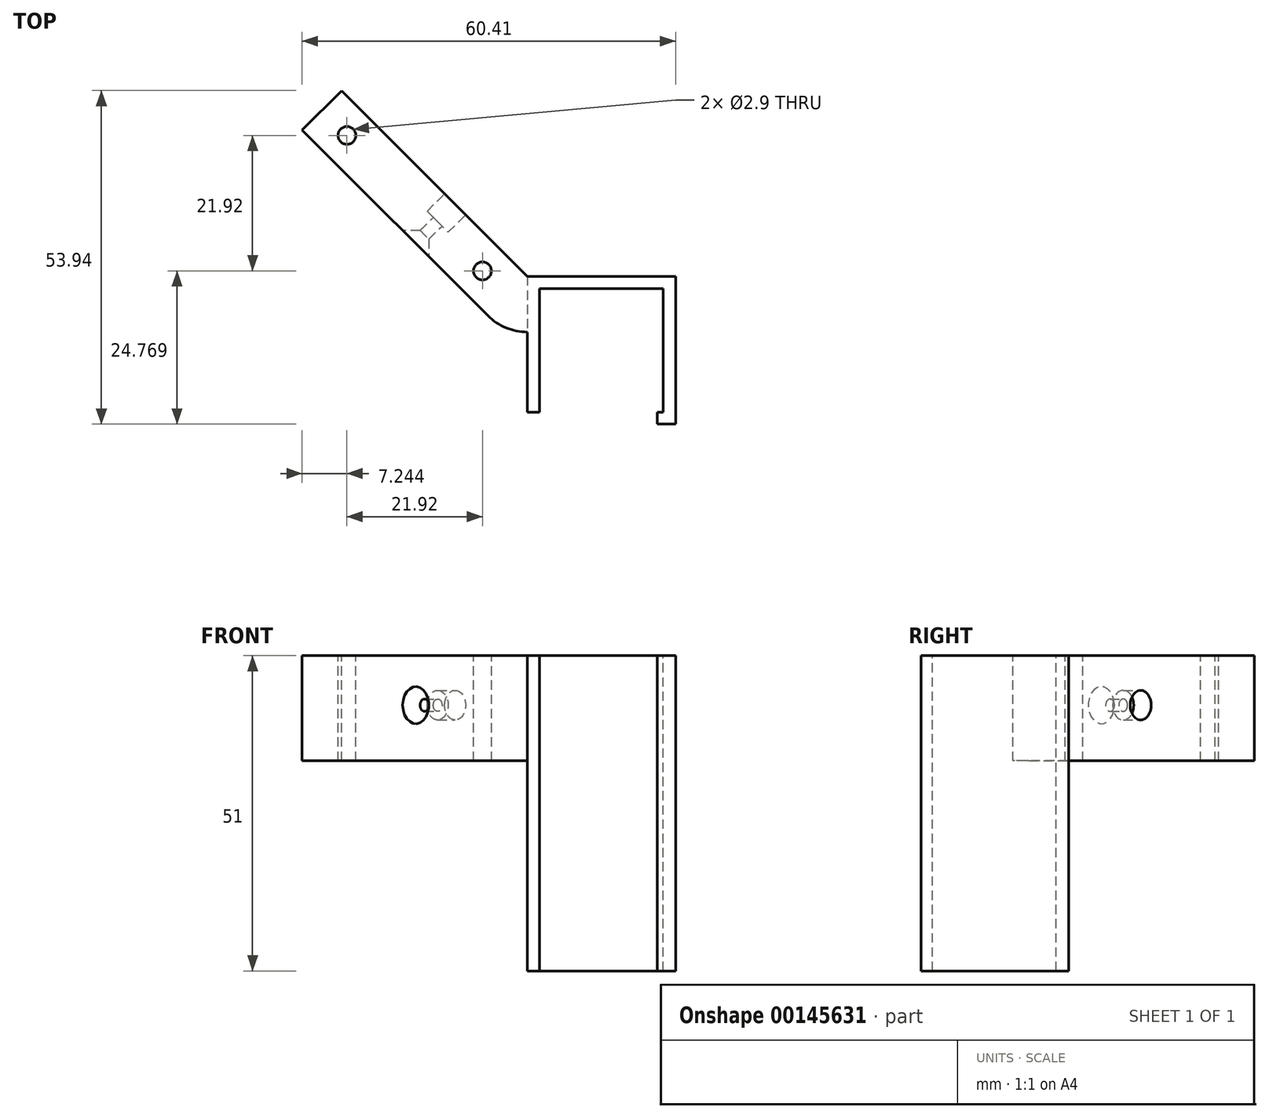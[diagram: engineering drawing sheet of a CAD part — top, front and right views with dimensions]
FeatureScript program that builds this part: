
annotation { "Feature Type Name" : "Feature", "Feature Type Description" : "" }
export const myFeature = defineFeature(function(context is Context, id is Id, definition is map)
    precondition{}
    {
        {
            var Q0;
            Q0=qCreatedBy(makeId("Top.planeOp"),FACE);
            var sketch = newSketch(context, id + "F0", { "sketchPlane" : qUnion([Q0])});
            skLineSegment(sketch, "E0", {"start": v(0.11, 9.4) * mm, "end": v(0.11, 0.4) * mm});
            skLineSegment(sketch, "E1", {"start": v(0.11, 0.4) * mm, "end": v(0.11, -12.6) * mm});
            skLineSegment(sketch, "E2", {"start": v(0.11, -12.6) * mm, "end": v(2.11, -12.6) * mm});
            skLineSegment(sketch, "E3", {"start": v(2.11, -12.6) * mm, "end": v(2.11, 7.4) * mm});
            skLineSegment(sketch, "E4", {"start": v(2.11, 7.4) * mm, "end": v(22.11, 7.4) * mm});
            skLineSegment(sketch, "E5", {"start": v(22.11, 7.4) * mm, "end": v(22.11, -12.6) * mm});
            skLineSegment(sketch, "E6", {"start": v(24.11, -12.6) * mm, "end": v(24.11, 9.4) * mm});
            skLineSegment(sketch, "E7", {"start": v(24.11, 9.4) * mm, "end": v(0.11, 9.4) * mm});
            skLineSegment(sketch, "E8", {"start": v(22.11, -12.6) * mm, "end": v(21.11, -12.6) * mm});
            skLineSegment(sketch, "E9", {"start": v(21.11, -12.6) * mm, "end": v(21.11, -14.48) * mm});
            skLineSegment(sketch, "E10", {"start": v(21.11, -14.48) * mm, "end": v(24.11, -14.48) * mm});
            skLineSegment(sketch, "E11", {"start": v(24.11, -14.48) * mm, "end": v(24.11, -12.6) * mm});
            skLineSegment(sketch, "E12", {"start": v(-29.94, 39.46) * mm, "end": v(0.11, 9.4) * mm});
            skLineSegment(sketch, "E13", {"start": v(0.11, 9.4) * mm, "end": v(-6.25, 3.04) * mm});
            skLineSegment(sketch, "E14", {"start": v(-6.25, 3.04) * mm, "end": v(-36.3, 33.1) * mm});
            skLineSegment(sketch, "E15", {"start": v(-36.3, 33.1) * mm, "end": v(-29.94, 39.46) * mm});
            skLineSegment(sketch, "E16", {"start": v(-33.12, 36.28) * mm, "end": v(-29.06, 32.2) * mm, "construction": true});
            skLineSegment(sketch, "E17", {"start": v(-29.06, 32.2) * mm, "end": v(-7.14, 10.29) * mm, "construction": true});
            skLineSegment(sketch, "E18", {"start": v(-7.14, 10.29) * mm, "end": v(-3.07, 6.22) * mm, "construction": true});
            skCircle(sketch, "E19", {"center": v(-29.06, 32.2) * mm, "radius": 1.45 * mm});
            skCircle(sketch, "E20", {"center": v(-7.14, 10.29) * mm, "radius": 1.45 * mm});
            skCircle(sketch, "E21", {"center": v(0.11, 9.4) * mm, "radius": 9 * mm});
            skSolve(sketch);
        }
        {
            var Q0;
            {var subQ1=sQuery(id+"F0.wireOp",EDGE,"E14");Q0=makeQuery(id+"F0.imprint","IMPRINT",FACE,{"disambiguationData":[TD([[makeQuery(id+"F0.imprint","IMPRINT",EDGE,{"derivedFrom":subQ1}),-1.0]])]});}
            var Q1;
            {var subQ0=sQuery(id+"F0.wireOp",EDGE,"E13");Q1=makeQuery(id+"F0.imprint","IMPRINT",FACE,{"disambiguationData":[TD([[makeQuery(id+"F0.imprint","IMPRINT",EDGE,{"derivedFrom":subQ0}),-1.0]])]});}
            var Q2;
            {var subQ0=sQuery(id+"F0.wireOp",EDGE,"E0");Q2=makeQuery(id+"F0.imprint","IMPRINT",FACE,{"disambiguationData":[TD([[makeQuery(id+"F0.imprint","IMPRINT",EDGE,{"derivedFrom":subQ0}),-1.0]])]});}
            var Q3;
            {var subQ1=sQuery(id+"F0.wireOp",EDGE,"E0");Q3=makeQuery(id+"F0.imprint","IMPRINT",FACE,{"disambiguationData":[TD([[makeQuery(id+"F0.imprint","IMPRINT",EDGE,{"derivedFrom":subQ1}),1.0]])]});}
            var Q4;
            {var subQ0=sQuery(id+"F0.wireOp",EDGE,"E1");Q4=makeQuery(id+"F0.imprint","IMPRINT",FACE,{"disambiguationData":[TD([[makeQuery(id+"F0.imprint","IMPRINT",EDGE,{"derivedFrom":subQ0}),1.0]])]});}
            var Q5;
            {var subQ4=sQuery(id+"F0.wireOp",EDGE,"E5");Q5=makeQuery(id+"F0.imprint","IMPRINT",FACE,{"disambiguationData":[TD([[makeQuery(id+"F0.imprint","IMPRINT",EDGE,{"derivedFrom":subQ4}),1.0]])]});}
            extrude(context, id + "F1", {"entities" : qUnion([Q0, Q1, Q2, Q3, Q4, Q5]), "oppositeDirection" : true, "depth" : 17 * mm});
        }
        {
            var Q0;
            {var subQ0=sQuery(id+"F0.wireOp",EDGE,"E1");Q0=makeQuery(id+"F0.imprint","IMPRINT",FACE,{"disambiguationData":[TD([[makeQuery(id+"F0.imprint","IMPRINT",EDGE,{"derivedFrom":subQ0}),1.0]])]});}
            var Q1;
            {var subQ1=sQuery(id+"F0.wireOp",EDGE,"E0");Q1=makeQuery(id+"F0.imprint","IMPRINT",FACE,{"disambiguationData":[TD([[makeQuery(id+"F0.imprint","IMPRINT",EDGE,{"derivedFrom":subQ1}),1.0]])]});}
            var Q2;
            {var subQ4=sQuery(id+"F0.wireOp",EDGE,"E5");Q2=makeQuery(id+"F0.imprint","IMPRINT",FACE,{"disambiguationData":[TD([[makeQuery(id+"F0.imprint","IMPRINT",EDGE,{"derivedFrom":subQ4}),1.0]])]});}
            extrude(context, id + "F2", {"entities" : qUnion([Q0, Q1, Q2]), "operationType" : NewBodyOperationType.ADD, "oppositeDirection" : true, "depth" : (17 + 34) * mm});
        }
        {
            var Q0;
            Q0=makeQuery(id+"F1.opExtrude","SWEPT_FACE",FACE,{"disambiguationData":[OSD([sQuery(id+"F0.wireOp",EDGE,"E12")])]});
            var sketch = newSketch(context, id + "F3", { "sketchPlane" : qUnion([Q0])});
            skLineSegment(sketch, "E22", {"start": v(23.07, 0) * mm, "end": v(23.07, -17) * mm, "construction": true});
            skLineSegment(sketch, "E23", {"start": v(49.07, -8) * mm, "end": v(6.57, -8) * mm, "construction": true});
            skPoint(sketch, "E24", {"position": v(23.07, -8) * mm});
            skCircle(sketch, "E25", {"center": v(23.07, -8) * mm, "radius": 2.4 * mm});
            skCircle(sketch, "E26", {"center": v(23.07, -8) * mm, "radius": 1 * mm});
            skSolve(sketch);
        }
        {
            var Q0;
            Q0=makeQuery(id+"F3.imprint","IMPRINT",FACE,{"disambiguationData":[TD([[makeQuery(id+"F3.imprint","IMPRINT",EDGE,{"derivedFrom":sQuery(id+"F3.wireOp",EDGE,"E26")}),1.0]])]});
            extrude(context, id + "F4", {"entities" : qUnion([Q0]), "operationType" : NewBodyOperationType.REMOVE, "endBound" : BoundingType.THROUGH_ALL, "oppositeDirection" : true, "depth" : 25 * mm});
        }
        {
            var Q0;
            Q0=makeQuery(id+"F3.imprint","IMPRINT",FACE,{"disambiguationData":[TD([[makeQuery(id+"F3.imprint","IMPRINT",EDGE,{"derivedFrom":sQuery(id+"F3.wireOp",EDGE,"E25")}),1.0]])]});
            extrude(context, id + "F5", {"entities" : qUnion([Q0]), "operationType" : NewBodyOperationType.REMOVE, "oppositeDirection" : true, "depth" : 4 * mm});
        }
        {
            var Q0;
            Q0=makeQuery(id+"F4.boolean.opBoolean","INTERSECT",EDGE,{"derivedFrom":[makeQuery(id+"F1.opExtrude","SWEPT_FACE",FACE,{"disambiguationData":[OSD([sQuery(id+"F0.wireOp",EDGE,"E14")])]}),makeQuery(id+"F4.opExtrude","SWEPT_FACE",FACE,{"disambiguationData":[OSD([sQuery(id+"F3.wireOp",EDGE,"E26")])]})]});
            chamfer(context, id + "F6", {"entities" : qUnion([Q0]), "width" : 2 * mm, "tangentPropagation" : true});
        }
    });
